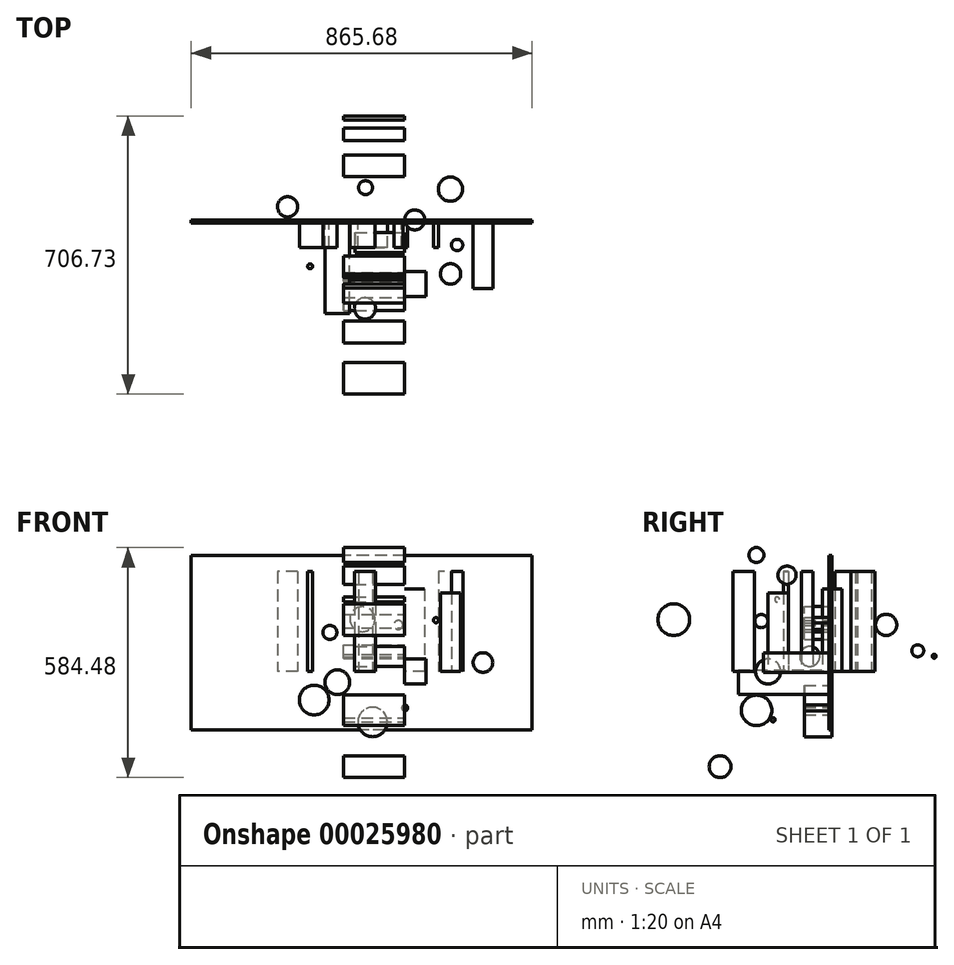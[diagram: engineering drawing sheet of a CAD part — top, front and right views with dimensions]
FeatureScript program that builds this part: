
annotation { "Feature Type Name" : "Feature", "Feature Type Description" : "" }
export const myFeature = defineFeature(function(context is Context, id is Id, definition is map)
    precondition{}
    {
        {
            var Q0;
            Q0=qCreatedBy(makeId("Top.planeOp"),FACE);
            var sketch = newSketch(context, id + "F0", { "sketchPlane" : qUnion([Q0])});
            skCircle(sketch, "E0", {"center": v(25.4, 0) * mm, "radius": 25.4 * mm});
            skSolve(sketch);
        }
        {
            var Q0;
            Q0 = qSketchRegion(id + "F0", true);
            extrude(context, id + "F1", {"entities" : qUnion([Q0]), "depth" : 209.84 * mm});
        }
        {
            var Q0;
            Q0=qCreatedBy(makeId("Right.planeOp"),FACE);
            var sketch = newSketch(context, id + "F2", { "sketchPlane" : qUnion([Q0])});
            skCircle(sketch, "E1", {"center": v(-57.04, 38.24) * mm, "radius": 25.4 * mm});
            skSolve(sketch);
        }
        {
            var Q0;
            Q0 = qSketchRegion(id + "F2", true);
            extrude(context, id + "F3", {"entities" : qUnion([Q0]), "oppositeDirection" : true, "depth" : 126.3 * mm});
        }
        {
            var Q0;
            Q0=qCreatedBy(makeId("Front.planeOp"),FACE);
            var sketch = newSketch(context, id + "F4", { "sketchPlane" : qUnion([Q0])});
            skCircle(sketch, "E2", {"center": v(198.68, 22.72) * mm, "radius": 25 * mm});
            skSolve(sketch);
        }
        {
            var Q0;
            Q0 = qSketchRegion(id + "F4", true);
            extrude(context, id + "F5", {"entities" : qUnion([Q0]), "depth" : 174.07 * mm});
        }
        {
            var Q0;
            Q0=qCreatedBy(makeId("Top.planeOp"),FACE);
            var sketch = newSketch(context, id + "F6", { "sketchPlane" : qUnion([Q0])});
            skCircle(sketch, "E3", {"center": v(116.34, -137.26) * mm, "radius": 25.95 * mm});
            skSolve(sketch);
        }
        {
            var Q0;
            Q0 = qSketchRegion(id + "F6", true);
            extrude(context, id + "F7", {"entities" : qUnion([Q0]), "depth" : 200.03 * mm});
        }
        {
            var Q0;
            Q0=qCreatedBy(makeId("Right.planeOp"),FACE);
            var sketch = newSketch(context, id + "F8", { "sketchPlane" : qUnion([Q0])});
            skCircle(sketch, "E4", {"center": v(-162.78, 0) * mm, "radius": 31.76 * mm});
            skSolve(sketch);
        }
        {
            var Q0;
            Q0 = qSketchRegion(id + "F8", true);
            extrude(context, id + "F9", {"entities" : qUnion([Q0]), "depth" : 54.58 * mm});
        }
        {
            var Q0;
            Q0=qCreatedBy(makeId("Front.planeOp"),FACE);
            var sketch = newSketch(context, id + "F10", { "sketchPlane" : qUnion([Q0])});
            skCircle(sketch, "E5", {"center": v(-171.1, -27.41) * mm, "radius": 31.46 * mm});
            skSolve(sketch);
        }
        {
            var Q0;
            Q0 = qSketchRegion(id + "F10", true);
            extrude(context, id + "F11", {"entities" : qUnion([Q0]), "depth" : 238.4 * mm});
        }
        {
            var Q0;
            Q0=qCreatedBy(makeId("Top.planeOp"),FACE);
            var sketch = newSketch(context, id + "F12", { "sketchPlane" : qUnion([Q0])});
            skCircle(sketch, "E6", {"center": v(-101.13, -225.02) * mm, "radius": 27.06 * mm});
            skCircle(sketch, "E7", {"center": v(116.04, 77.97) * mm, "radius": 30.8 * mm});
            skCircle(sketch, "E8", {"center": v(-297.59, 33.16) * mm, "radius": 25.6 * mm});
            skCircle(sketch, "E9", {"center": v(-99.6, 81.78) * mm, "radius": 17.77 * mm});
            skCircle(sketch, "E10", {"center": v(133.06, -63.94) * mm, "radius": 14.5 * mm});
            skCircle(sketch, "E11", {"center": v(-240.25, -118.03) * mm, "radius": 6.31 * mm});
            skSolve(sketch);
        }
        {
            var Q0;
            Q0 = qSketchRegion(id + "F12", true);
            extrude(context, id + "F13", {"entities" : qUnion([Q0]), "depth" : 254.32 * mm});
        }
        {
            var Q0;
            Q0=qCreatedBy(makeId("Front.planeOp"),FACE);
            var sketch = newSketch(context, id + "F14", { "sketchPlane" : qUnion([Q0])});
            skCircle(sketch, "E12", {"center": v(-16.1, 118.23) * mm, "radius": 11.32 * mm});
            skCircle(sketch, "E13", {"center": v(79.25, 130.37) * mm, "radius": 6.54 * mm});
            skCircle(sketch, "E14", {"center": v(-190.22, 99.2) * mm, "radius": 17.84 * mm});
            skCircle(sketch, "E15", {"center": v(-229.95, -72.5) * mm, "radius": 37.7 * mm});
            skCircle(sketch, "E16", {"center": v(0, -92.56) * mm, "radius": 7.57 * mm});
            skCircle(sketch, "E17", {"center": v(-81.62, -128.3) * mm, "radius": 37.35 * mm});
            skCircle(sketch, "E18", {"center": v(-107.55, 132.92) * mm, "radius": 31.8 * mm});
            skSolve(sketch);
        }
        {
            var Q0;
            Q0 = qSketchRegion(id + "F14", true);
            extrude(context, id + "F15", {"entities" : qUnion([Q0]), "depth" : 70.84 * mm});
        }
        {
            var Q0;
            Q0=qCreatedBy(makeId("Right.planeOp"),FACE);
            var sketch = newSketch(context, id + "F16", { "sketchPlane" : qUnion([Q0])});
            skCircle(sketch, "E19", {"center": v(137.07, 118.44) * mm, "radius": 27 * mm});
            skCircle(sketch, "E20", {"center": v(217.36, 52.72) * mm, "radius": 15.3 * mm});
            skCircle(sketch, "E21", {"center": v(259.1, 38.79) * mm, "radius": 5.02 * mm});
            skCircle(sketch, "E22", {"center": v(-402.4, 131.75) * mm, "radius": 40.2 * mm});
            skCircle(sketch, "E23", {"center": v(-192.61, 295.86) * mm, "radius": 19.02 * mm});
            skCircle(sketch, "E24", {"center": v(-284.8, -241.85) * mm, "radius": 27.75 * mm});
            skCircle(sketch, "E25", {"center": v(-192.19, -98.83) * mm, "radius": 38.77 * mm});
            skCircle(sketch, "E26", {"center": v(-150.26, -122.76) * mm, "radius": 5.23 * mm});
            skCircle(sketch, "E27", {"center": v(-180.09, 127.9) * mm, "radius": 16.72 * mm});
            skCircle(sketch, "E28", {"center": v(-139.94, 182.82) * mm, "radius": 6.17 * mm});
            skCircle(sketch, "E29", {"center": v(-114.7, 244.8) * mm, "radius": 23.14 * mm});
            skSolve(sketch);
        }
        {
            var Q0;
            Q0 = qSketchRegion(id + "F16", true);
            extrude(context, id + "F17", {"entities" : qUnion([Q0]), "oppositeDirection" : true, "depth" : 156.1 * mm});
        }
        {
            var Q0;
            Q0=qCreatedBy(makeId("Front.planeOp"),FACE);
            var sketch = newSketch(context, id + "F18", { "sketchPlane" : qUnion([Q0])});
            skLineSegment(sketch, "E30.bottom", {"start": v(323.38, -148.74) * mm, "end": v(-542.3, -148.74) * mm});
            skLineSegment(sketch, "E30.top", {"start": v(323.38, 294.75) * mm, "end": v(-542.3, 294.75) * mm});
            skLineSegment(sketch, "E30.left", {"start": v(323.38, -148.74) * mm, "end": v(323.38, 294.75) * mm});
            skLineSegment(sketch, "E30.right", {"start": v(-542.3, -148.74) * mm, "end": v(-542.3, 294.75) * mm});
            skSolve(sketch);
        }
        {
            var Q0;
            Q0 = qSketchRegion(id + "F18", true);
            extrude(context, id + "F19", {"entities" : qUnion([Q0]), "depth" : 8.7 * mm});
        }
    });
